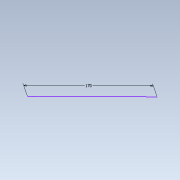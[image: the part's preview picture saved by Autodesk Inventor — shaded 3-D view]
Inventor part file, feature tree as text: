
AUTODESK INVENTOR PART (.ipt)
format: ipt  version: 2021 (Build 250183000, 183)  size: 63,488 bytes
history: native  units: mm
features: sketch x1
ambient origin geometry x8: Origin, YZ Plane, XZ Plane, XY Plane, X Axis, Y Axis, Z Axis, Center Point
feature tree (1):
  sketch  "Sketch1"  dims[d0=170.0mm]
